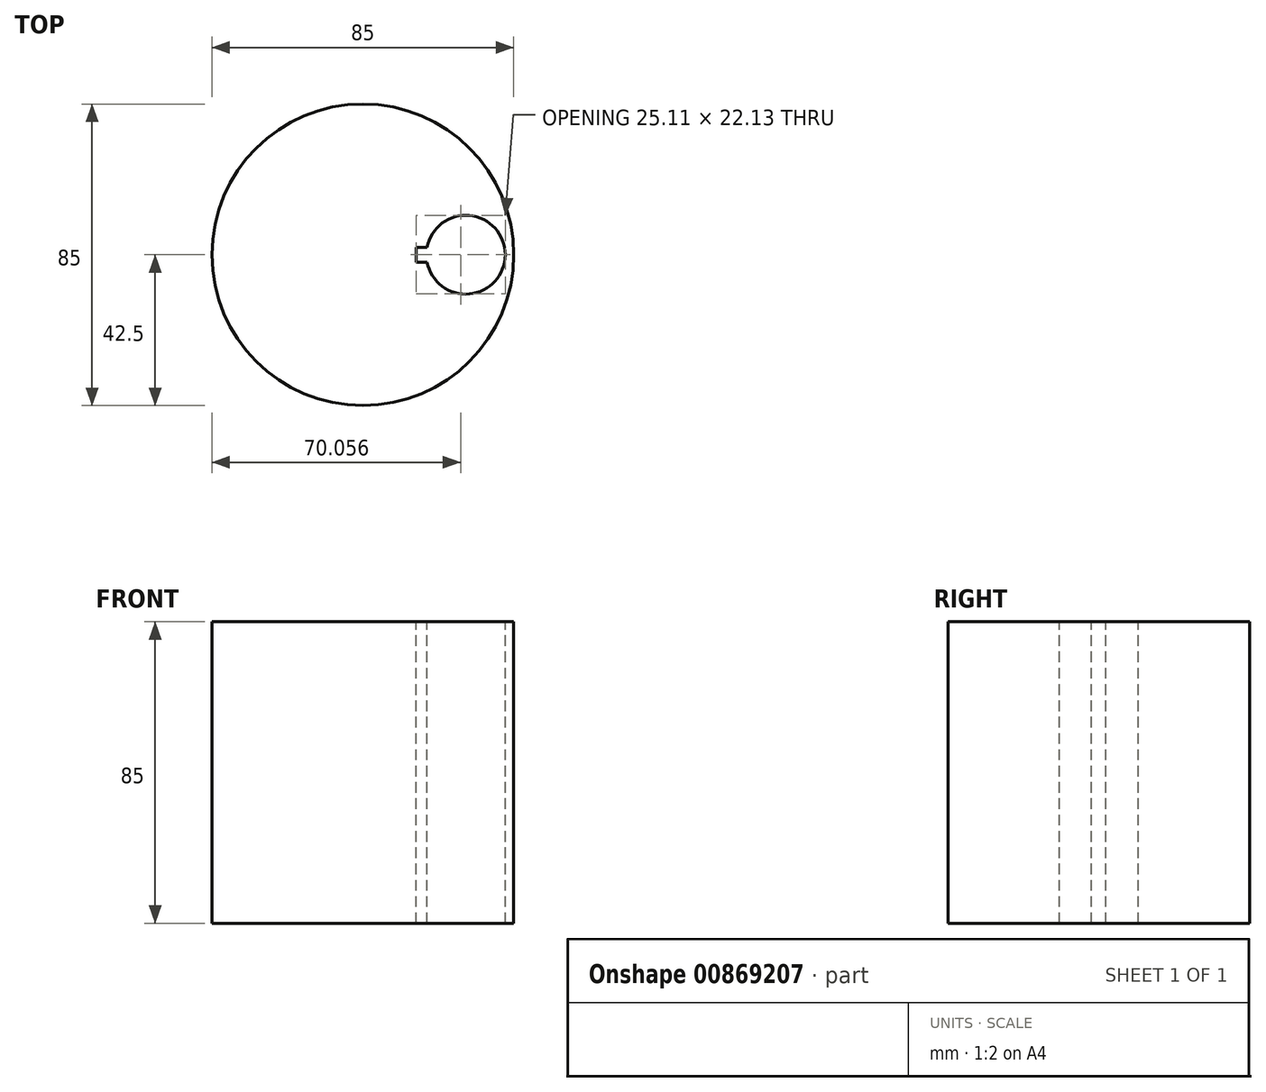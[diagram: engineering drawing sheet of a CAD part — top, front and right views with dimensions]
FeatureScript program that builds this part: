
annotation { "Feature Type Name" : "Feature", "Feature Type Description" : "" }
export const myFeature = defineFeature(function(context is Context, id is Id, definition is map)
    precondition{}
    {
        {
            var Q0;
            Q0=qCreatedBy(makeId("Top.planeOp"),FACE);
            var sketch = newSketch(context, id + "F0", { "sketchPlane" : qUnion([Q0])});
            skCircle(sketch, "E0", {"center": v(0, 0) * mm, "radius": 42.5 * mm});
            skSolve(sketch);
        }
        {
            var Q0;
            Q0=makeQuery(id+"F0.imprint","IMPRINT",FACE,{"disambiguationData":[TD([[makeQuery(id+"F0.imprint","IMPRINT",EDGE,{"derivedFrom":sQuery(id+"F0.wireOp",EDGE,"E0")}),1.0]])]});
            extrude(context, id + "F1", {"entities" : qUnion([Q0]), "flatOperationType" : FlatOperationType.REMOVE, "depth" : (85) * mm, "offsetDistance" : 25 * mm, "domain" : OperationDomain.MODEL});
        }
        {
            var Q0;
            Q0=makeQuery(id+"F1.opExtrude","CAP_FACE",FACE,{"disambiguationData":[OSD([sQuery(id+"F0.wireOp",EDGE,"E0")])],"isStart":false});
            var sketch = newSketch(context, id + "F2", { "sketchPlane" : qUnion([Q0])});
            skArc(sketch, "E1", {"start": v(18.08, -2.05) * mm, "mid": v(40.11, 0) * mm, "end": v(18.08, 2.05) * mm});
            skCircle(sketch, "E2", {"center": v(0, 0) * mm, "radius": 29 * mm, "construction": true});
            skLineSegment(sketch, "E3", {"start": v(18.08, 2.05) * mm, "end": v(15, 2.05) * mm});
            skLineSegment(sketch, "E4", {"start": v(15, 2.05) * mm, "end": v(15, -2.05) * mm});
            skLineSegment(sketch, "E5", {"start": v(15, -2.05) * mm, "end": v(18.08, -2.05) * mm});
            skSolve(sketch);
        }
        {
            var Q0;
            Q0=makeQuery(id+"F2.imprint","IMPRINT",FACE,{"disambiguationData":[TD([[makeQuery(id+"F2.imprint","IMPRINT",EDGE,{"derivedFrom":sQuery(id+"F2.wireOp",EDGE,"E1")}),1.0]])]});
            extrude(context, id + "F3", {"entities" : qUnion([Q0]), "operationType" : NewBodyOperationType.REMOVE, "endBound" : BoundingType.THROUGH_ALL, "oppositeDirection" : true, "depth" : 25 * mm, "offsetDistance" : 25 * mm});
        }
    });
